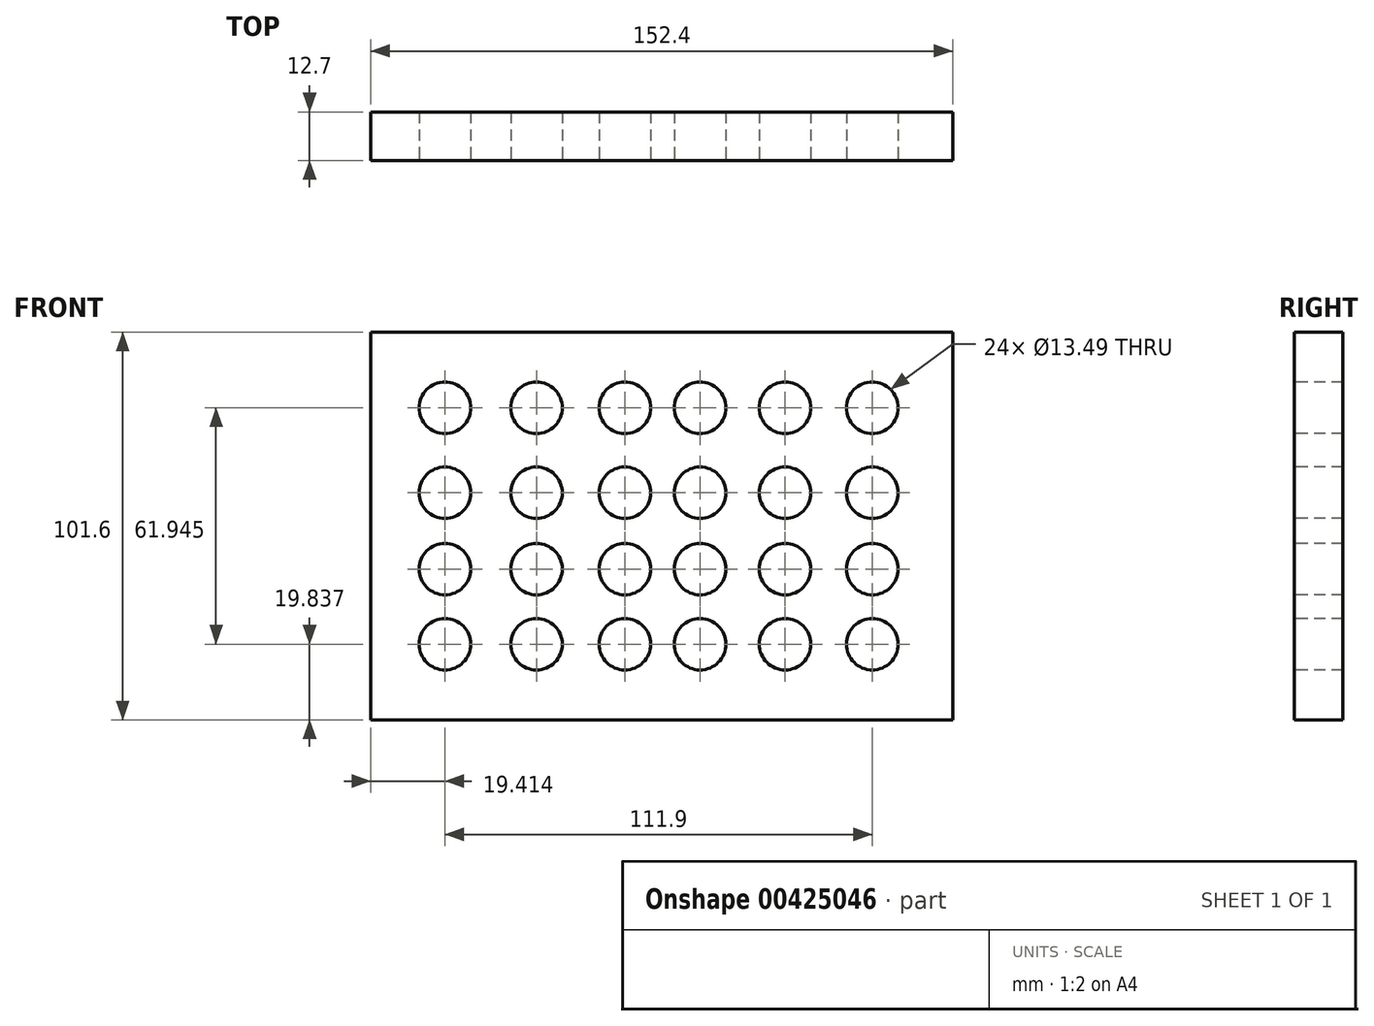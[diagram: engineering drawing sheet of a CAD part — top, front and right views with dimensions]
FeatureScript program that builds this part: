
annotation { "Feature Type Name" : "Feature", "Feature Type Description" : "" }
export const myFeature = defineFeature(function(context is Context, id is Id, definition is map)
    precondition{}
    {
        {
            var Q0;
            Q0=qCreatedBy(makeId("Front.planeOp"),FACE);
            var sketch = newSketch(context, id + "F0", { "sketchPlane" : qUnion([Q0])});
            skLineSegment(sketch, "E0", {"start": v(-73.96, 0) * mm, "end": v(78.44, 0) * mm});
            skLineSegment(sketch, "E1", {"start": v(78.44, 0) * mm, "end": v(78.44, 101.6) * mm});
            skLineSegment(sketch, "E2", {"start": v(78.44, 101.6) * mm, "end": v(-73.96, 101.6) * mm});
            skLineSegment(sketch, "E3", {"start": v(-73.96, 101.6) * mm, "end": v(-73.96, 0) * mm});
            skSolve(sketch);
        }
        {
            var Q0;
            Q0=makeQuery(id+"F0.imprint","IMPRINT",FACE,{"disambiguationData":[TD([[makeQuery(id+"F0.imprint","IMPRINT",EDGE,{"derivedFrom":sQuery(id+"F0.wireOp",EDGE,"E0")}),1.0]])]});
            extrude(context, id + "F1", {"entities" : qUnion([Q0]), "depth" : 12.7 * mm});
        }
        {
            var Q0;
            Q0=makeQuery(id+"F1.opExtrude","CAP_FACE",FACE,{"disambiguationData":[OSD([sQuery(id+"F0.wireOp",EDGE,"E0"),sQuery(id+"F0.wireOp",EDGE,"E1"),sQuery(id+"F0.wireOp",EDGE,"E2"),sQuery(id+"F0.wireOp",EDGE,"E3")])],"isStart":false});
            var sketch = newSketch(context, id + "F2", { "sketchPlane" : qUnion([Q0])});
            skPoint(sketch, "E4", {"position": v(-73.96, 81.78) * mm});
            skPoint(sketch, "E5", {"position": v(-73.96, 59.52) * mm});
            skPoint(sketch, "E6", {"position": v(-73.96, 39.53) * mm});
            skPoint(sketch, "E7", {"position": v(-73.96, 19.84) * mm});
            skLineSegment(sketch, "E8", {"start": v(-73.96, 81.78) * mm, "end": v(78.44, 81.78) * mm});
            skLineSegment(sketch, "E9", {"start": v(78.44, 81.78) * mm, "end": v(-73.96, 81.78) * mm});
            skLineSegment(sketch, "E10", {"start": v(-73.96, 59.52) * mm, "end": v(78.44, 59.52) * mm});
            skLineSegment(sketch, "E11", {"start": v(78.44, 59.52) * mm, "end": v(-73.96, 59.52) * mm});
            skLineSegment(sketch, "E12", {"start": v(-73.96, 39.53) * mm, "end": v(78.44, 39.53) * mm});
            skLineSegment(sketch, "E13", {"start": v(78.44, 39.53) * mm, "end": v(-73.96, 39.53) * mm});
            skLineSegment(sketch, "E14", {"start": v(-73.96, 19.84) * mm, "end": v(78.44, 19.84) * mm});
            skLineSegment(sketch, "E15", {"start": v(78.44, 19.84) * mm, "end": v(-73.96, 19.84) * mm});
            skPoint(sketch, "E16", {"position": v(-54.55, 81.78) * mm});
            skPoint(sketch, "E17", {"position": v(34.52, 81.78) * mm});
            skPoint(sketch, "E18", {"position": v(12.25, 81.78) * mm});
            skPoint(sketch, "E19", {"position": v(-7.45, 81.78) * mm});
            skPoint(sketch, "E20", {"position": v(-30.57, 81.78) * mm});
            skPoint(sketch, "E21", {"position": v(-54.55, 59.52) * mm});
            skPoint(sketch, "E22", {"position": v(-54.55, 39.53) * mm});
            skPoint(sketch, "E23", {"position": v(-54.55, 19.84) * mm});
            skPoint(sketch, "E24", {"position": v(-30.57, 59.52) * mm});
            skPoint(sketch, "E25", {"position": v(-30.57, 39.53) * mm});
            skPoint(sketch, "E26", {"position": v(-30.57, 19.84) * mm});
            skPoint(sketch, "E27", {"position": v(-7.45, 59.52) * mm});
            skPoint(sketch, "E28", {"position": v(-7.45, 39.53) * mm});
            skPoint(sketch, "E29", {"position": v(-7.45, 19.84) * mm});
            skPoint(sketch, "E30", {"position": v(12.25, 59.52) * mm});
            skPoint(sketch, "E31", {"position": v(12.25, 39.53) * mm});
            skPoint(sketch, "E32", {"position": v(12.25, 19.84) * mm});
            skPoint(sketch, "E33", {"position": v(34.52, 59.52) * mm});
            skPoint(sketch, "E34", {"position": v(34.52, 39.53) * mm});
            skPoint(sketch, "E35", {"position": v(34.52, 19.84) * mm});
            skPoint(sketch, "E36", {"position": v(57.35, 81.78) * mm});
            skPoint(sketch, "E37", {"position": v(57.35, 59.52) * mm});
            skPoint(sketch, "E38", {"position": v(57.35, 39.53) * mm});
            skPoint(sketch, "E39", {"position": v(57.35, 19.84) * mm});
            skSolve(sketch);
        }
        {
            var Q0;
            Q0=sQuery(id+"F2.wireOp",VERTEX,"E16");
            var Q1;
            Q1=sQuery(id+"F2.wireOp",VERTEX,"E21");
            var Q2;
            Q2=sQuery(id+"F2.wireOp",VERTEX,"E22");
            var Q3;
            Q3=sQuery(id+"F2.wireOp",VERTEX,"E19");
            var Q4;
            Q4=sQuery(id+"F2.wireOp",VERTEX,"E27");
            var Q5;
            Q5=sQuery(id+"F2.wireOp",VERTEX,"E28");
            var Q6;
            Q6=sQuery(id+"F2.wireOp",VERTEX,"E29");
            var Q7;
            Q7=sQuery(id+"F2.wireOp",VERTEX,"E20");
            var Q8;
            Q8=sQuery(id+"F2.wireOp",VERTEX,"E24");
            var Q9;
            Q9=sQuery(id+"F2.wireOp",VERTEX,"E25");
            var Q10;
            Q10=sQuery(id+"F2.wireOp",VERTEX,"E26");
            var Q11;
            Q11=sQuery(id+"F2.wireOp",VERTEX,"E23");
            var Q12;
            Q12=sQuery(id+"F2.wireOp",VERTEX,"E18");
            var Q13;
            Q13=sQuery(id+"F2.wireOp",VERTEX,"E30");
            var Q14;
            Q14=sQuery(id+"F2.wireOp",VERTEX,"E31");
            var Q15;
            Q15=sQuery(id+"F2.wireOp",VERTEX,"E32");
            var Q16;
            Q16=sQuery(id+"F2.wireOp",VERTEX,"E35");
            var Q17;
            Q17=sQuery(id+"F2.wireOp",VERTEX,"E34");
            var Q18;
            Q18=sQuery(id+"F2.wireOp",VERTEX,"E33");
            var Q19;
            Q19=sQuery(id+"F2.wireOp",VERTEX,"E17");
            var Q20;
            Q20=sQuery(id+"F2.wireOp",VERTEX,"E36");
            var Q21;
            Q21=sQuery(id+"F2.wireOp",VERTEX,"E37");
            var Q22;
            Q22=sQuery(id+"F2.wireOp",VERTEX,"E38");
            var Q23;
            Q23=sQuery(id+"F2.wireOp",VERTEX,"E39");
            var Q24;
            Q24=makeQuery(id+"F1.opExtrude","SWEPT_BODY",BODY,{"disambiguationData":[OSD([sQuery(id+"F0.wireOp",EDGE,"E0"),sQuery(id+"F0.wireOp",EDGE,"E1"),sQuery(id+"F0.wireOp",EDGE,"E2"),sQuery(id+"F0.wireOp",EDGE,"E3")])]});
            hole(context, id + "F3", {"style" : HoleStyle.SIMPLE, "endStyle" : HoleEndStyle.THROUGH, "holeDiameter" : 13.5 * mm, "isTappedThrough" : true, "tappedDepth" : 12.7 * mm, "tapClearance" : 3, "locations" : qUnion([Q0, Q1, Q2, Q3, Q4, Q5, Q6, Q7, Q8, Q9, Q10, Q11, Q12, Q13, Q14, Q15, Q16, Q17, Q18, Q19, Q20, Q21, Q22, Q23]), "scope" : qUnion([Q24])});
        }
    });
